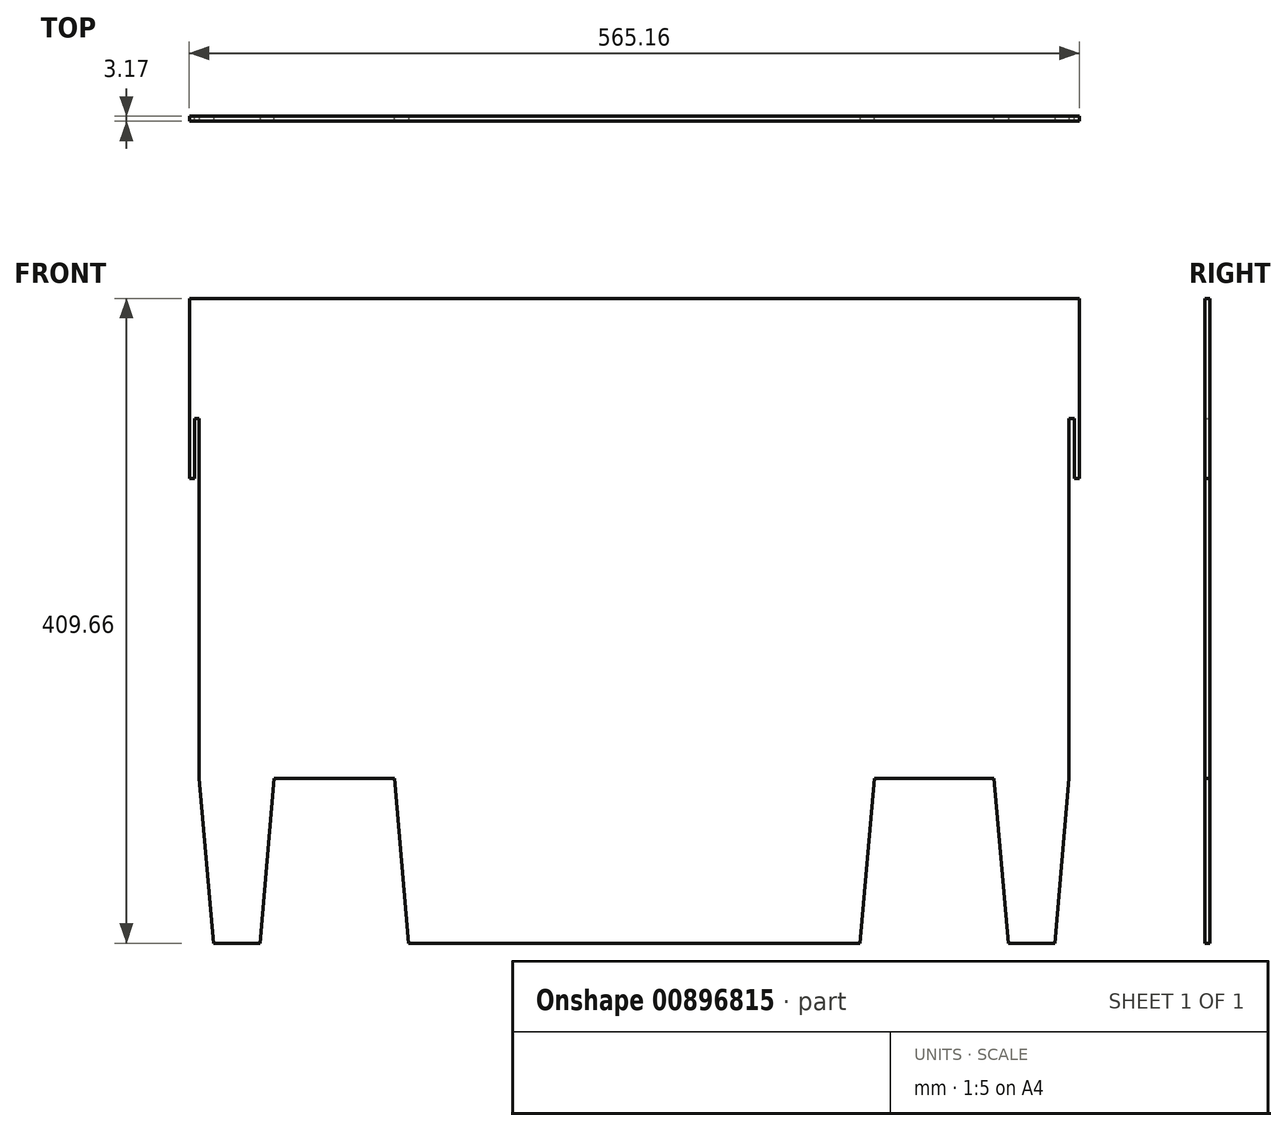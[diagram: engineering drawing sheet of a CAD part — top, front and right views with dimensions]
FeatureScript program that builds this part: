
annotation { "Feature Type Name" : "Feature", "Feature Type Description" : "" }
export const myFeature = defineFeature(function(context is Context, id is Id, definition is map)
    precondition{}
    {
        {
            var Q0;
            Q0=qCreatedBy(makeId("Front.planeOp"),FACE);
            var sketch = newSketch(context, id + "F0", { "sketchPlane" : qUnion([Q0])});
            skLineSegment(sketch, "E0.bottom", {"start": v(276.23, -304.8) * mm, "end": v(228.6, -304.8) * mm});
            skLineSegment(sketch, "E0.left", {"start": v(276.23, -304.8) * mm, "end": v(276.23, 190.5) * mm});
            skLineSegment(sketch, "E0.right", {"start": v(-276.23, -304.8) * mm, "end": v(-276.23, 190.5) * mm});
            skPoint(sketch, "E0.middle", {"position": v(0, 0) * mm});
            skLineSegment(sketch, "E1.top", {"start": v(-228.6, -38.1) * mm, "end": v(-152.4, -38.1) * mm});
            skLineSegment(sketch, "E1.left", {"start": v(-228.6, -304.8) * mm, "end": v(-228.6, -38.1) * mm});
            skLineSegment(sketch, "E1.right", {"start": v(-152.4, -304.8) * mm, "end": v(-152.4, -38.1) * mm});
            skLineSegment(sketch, "E2.top", {"start": v(152.4, -38.1) * mm, "end": v(228.6, -38.1) * mm});
            skLineSegment(sketch, "E2.left", {"start": v(152.4, -304.8) * mm, "end": v(152.4, -38.1) * mm});
            skLineSegment(sketch, "E2.right", {"start": v(228.6, -304.8) * mm, "end": v(228.6, -38.1) * mm});
            skLineSegment(sketch, "E3.trimOffspring", {"start": v(-228.6, -304.8) * mm, "end": v(-276.23, -304.8) * mm});
            skLineSegment(sketch, "E4.trimOffspring", {"start": v(152.4, -304.8) * mm, "end": v(-152.4, -304.8) * mm});
            skLineSegment(sketch, "E5.bottom", {"start": v(276.23, 266.7) * mm, "end": v(-276.23, 266.7) * mm});
            skPoint(sketch, "E0.top.start.orphan", {"position": v(276.22, 304.8) * mm});
            skPoint(sketch, "E6.orphan", {"position": v(-276.23, 304.8) * mm});
            skLineSegment(sketch, "E7.bottom", {"start": v(276.23, 266.7) * mm, "end": v(279.4, 266.7) * mm});
            skLineSegment(sketch, "E7.top", {"start": v(276.23, 190.5) * mm, "end": v(279.4, 190.5) * mm});
            skLineSegment(sketch, "E7.right", {"start": v(279.4, 266.7) * mm, "end": v(279.4, 190.5) * mm});
            skLineSegment(sketch, "E8.bottom", {"start": v(-276.23, 266.7) * mm, "end": v(-279.4, 266.7) * mm});
            skLineSegment(sketch, "E8.left", {"start": v(-276.23, 190.5) * mm, "end": v(-276.23, 185.04) * mm});
            skLineSegment(sketch, "E8.right", {"start": v(-279.4, 266.7) * mm, "end": v(-279.4, 190.5) * mm});
            skLineSegment(sketch, "E9", {"start": v(-279.4, 190.5) * mm, "end": v(-276.23, 190.5) * mm});
            skSolve(sketch);
        }
        {
            var Q0;
            Q0 = qSketchRegion(id + "F0", true);
            extrude(context, id + "F1", {"entities" : qUnion([Q0]), "depth" : 3.17 * mm, "offsetDistance" : 25.4 * mm});
        }
        {
            var Q0;
            Q0=makeQuery(id+"F1.opExtrude","CAP_FACE",FACE,{"disambiguationData":[OSD([sQuery(id+"F0.wireOp",EDGE,"E0.bottom"),sQuery(id+"F0.wireOp",EDGE,"E0.left"),sQuery(id+"F0.wireOp",EDGE,"E0.right"),sQuery(id+"F0.wireOp",EDGE,"E1.top"),sQuery(id+"F0.wireOp",EDGE,"E1.left"),sQuery(id+"F0.wireOp",EDGE,"E1.right"),sQuery(id+"F0.wireOp",EDGE,"E2.top"),sQuery(id+"F0.wireOp",EDGE,"E2.left"),sQuery(id+"F0.wireOp",EDGE,"E2.right"),sQuery(id+"F0.wireOp",EDGE,"E3.trimOffspring"),sQuery(id+"F0.wireOp",EDGE,"E4.trimOffspring"),sQuery(id+"F0.wireOp",EDGE,"E5.bottom"),sQuery(id+"F0.wireOp",EDGE,"E7.bottom"),sQuery(id+"F0.wireOp",EDGE,"E7.top"),sQuery(id+"F0.wireOp",EDGE,"E7.right"),sQuery(id+"F0.wireOp",EDGE,"E8.bottom"),sQuery(id+"F0.wireOp",EDGE,"E8.left"),sQuery(id+"F0.wireOp",EDGE,"E8.right"),sQuery(id+"F0.wireOp",EDGE,"E9")])],"isStart":false});
            var sketch = newSketch(context, id + "F2", { "sketchPlane" : qUnion([Q0])});
            skLineSegment(sketch, "E10.0.0", {"start": v(-276.23, 190.5) * mm, "end": v(-276.23, -304.8) * mm, "construction": true});
            skLineSegment(sketch, "E10.0.1", {"start": v(-276.23, -304.8) * mm, "end": v(-228.6, -304.8) * mm, "construction": true});
            skLineSegment(sketch, "E10.0.2", {"start": v(-228.6, -304.8) * mm, "end": v(-228.6, -38.1) * mm, "construction": true});
            skLineSegment(sketch, "E10.0.3", {"start": v(-228.6, -38.1) * mm, "end": v(-152.4, -38.1) * mm, "construction": true});
            skLineSegment(sketch, "E10.0.4", {"start": v(-152.4, -38.1) * mm, "end": v(-152.4, -304.8) * mm, "construction": true});
            skLineSegment(sketch, "E10.0.5", {"start": v(-152.4, -304.8) * mm, "end": v(152.4, -304.8) * mm, "construction": true});
            skLineSegment(sketch, "E10.0.6", {"start": v(152.4, -304.8) * mm, "end": v(152.4, -38.1) * mm, "construction": true});
            skLineSegment(sketch, "E10.0.7", {"start": v(152.4, -38.1) * mm, "end": v(228.6, -38.1) * mm, "construction": true});
            skLineSegment(sketch, "E10.0.8", {"start": v(228.6, -38.1) * mm, "end": v(228.6, -304.8) * mm, "construction": true});
            skLineSegment(sketch, "E10.0.9", {"start": v(228.6, -304.8) * mm, "end": v(276.23, -304.8) * mm, "construction": true});
            skLineSegment(sketch, "E10.0.10", {"start": v(276.23, -304.8) * mm, "end": v(276.23, 190.5) * mm, "construction": true});
            skLineSegment(sketch, "E10.0.11", {"start": v(276.23, 190.5) * mm, "end": v(279.4, 190.5) * mm, "construction": true});
            skLineSegment(sketch, "E10.0.12", {"start": v(279.4, 190.5) * mm, "end": v(279.4, 266.7) * mm, "construction": true});
            skLineSegment(sketch, "E10.0.13", {"start": v(279.4, 266.7) * mm, "end": v(-279.4, 266.7) * mm, "construction": true});
            skLineSegment(sketch, "E10.0.14", {"start": v(-279.4, 266.7) * mm, "end": v(-279.4, 190.5) * mm, "construction": true});
            skLineSegment(sketch, "E10.0.15", {"start": v(-279.4, 190.5) * mm, "end": v(-276.23, 190.5) * mm, "construction": true});
            skLineSegment(sketch, "E11.bottom", {"start": v(279.4, 266.7) * mm, "end": v(282.57, 266.7) * mm});
            skLineSegment(sketch, "E11.top", {"start": v(279.4, 152.4) * mm, "end": v(282.57, 152.4) * mm});
            skLineSegment(sketch, "E11.left", {"start": v(279.4, 266.7) * mm, "end": v(279.4, 152.4) * mm});
            skLineSegment(sketch, "E11.right", {"start": v(282.57, 266.7) * mm, "end": v(282.57, 152.4) * mm});
            skLineSegment(sketch, "E12.bottom", {"start": v(-279.4, 266.7) * mm, "end": v(-282.58, 266.7) * mm});
            skLineSegment(sketch, "E12.top", {"start": v(-279.4, 152.4) * mm, "end": v(-282.58, 152.4) * mm});
            skLineSegment(sketch, "E12.left", {"start": v(-279.4, 266.7) * mm, "end": v(-279.4, 152.4) * mm});
            skLineSegment(sketch, "E12.right", {"start": v(-282.58, 266.7) * mm, "end": v(-282.58, 152.4) * mm});
            skSolve(sketch);
        }
        {
            var Q0;
            Q0 = qSketchRegion(id + "F2", true);
            var Q1;
            Q1=makeQuery(id+"F1.opExtrude","CAP_FACE",FACE,{"disambiguationData":[OSD([sQuery(id+"F0.wireOp",EDGE,"E0.bottom"),sQuery(id+"F0.wireOp",EDGE,"E0.left"),sQuery(id+"F0.wireOp",EDGE,"E0.right"),sQuery(id+"F0.wireOp",EDGE,"E1.top"),sQuery(id+"F0.wireOp",EDGE,"E1.left"),sQuery(id+"F0.wireOp",EDGE,"E1.right"),sQuery(id+"F0.wireOp",EDGE,"E2.top"),sQuery(id+"F0.wireOp",EDGE,"E2.left"),sQuery(id+"F0.wireOp",EDGE,"E2.right"),sQuery(id+"F0.wireOp",EDGE,"E3.trimOffspring"),sQuery(id+"F0.wireOp",EDGE,"E4.trimOffspring"),sQuery(id+"F0.wireOp",EDGE,"E5.bottom"),sQuery(id+"F0.wireOp",EDGE,"E7.bottom"),sQuery(id+"F0.wireOp",EDGE,"E7.top"),sQuery(id+"F0.wireOp",EDGE,"E7.right"),sQuery(id+"F0.wireOp",EDGE,"E8.bottom"),sQuery(id+"F0.wireOp",EDGE,"E8.left"),sQuery(id+"F0.wireOp",EDGE,"E8.right"),sQuery(id+"F0.wireOp",EDGE,"E9")])],"isStart":true});
            extrude(context, id + "F3", {"entities" : qUnion([Q0]), "operationType" : NewBodyOperationType.ADD, "endBound" : BoundingType.UP_TO_SURFACE, "oppositeDirection" : true, "depth" : 25.4 * mm, "endBoundEntityFace" : qUnion([Q1]), "offsetDistance" : 25.4 * mm});
        }
        {
            var Q0;
            Q0=makeQuery(id+"F3.boolean.opBoolean","MERGE",FACE,{"derivedFrom":[makeQuery(id+"F1.opExtrude","CAP_FACE",FACE,{"disambiguationData":[OSD([sQuery(id+"F0.wireOp",EDGE,"E0.bottom"),sQuery(id+"F0.wireOp",EDGE,"E0.left"),sQuery(id+"F0.wireOp",EDGE,"E0.right"),sQuery(id+"F0.wireOp",EDGE,"E1.top"),sQuery(id+"F0.wireOp",EDGE,"E1.left"),sQuery(id+"F0.wireOp",EDGE,"E1.right"),sQuery(id+"F0.wireOp",EDGE,"E2.top"),sQuery(id+"F0.wireOp",EDGE,"E2.left"),sQuery(id+"F0.wireOp",EDGE,"E2.right"),sQuery(id+"F0.wireOp",EDGE,"E3.trimOffspring"),sQuery(id+"F0.wireOp",EDGE,"E4.trimOffspring"),sQuery(id+"F0.wireOp",EDGE,"E5.bottom"),sQuery(id+"F0.wireOp",EDGE,"E7.bottom"),sQuery(id+"F0.wireOp",EDGE,"E7.top"),sQuery(id+"F0.wireOp",EDGE,"E7.right"),sQuery(id+"F0.wireOp",EDGE,"E8.bottom"),sQuery(id+"F0.wireOp",EDGE,"E8.left"),sQuery(id+"F0.wireOp",EDGE,"E8.right"),sQuery(id+"F0.wireOp",EDGE,"E9")])],"isStart":false}),makeQuery(id+"F3.opExtrude","CAP_FACE",FACE,{"disambiguationData":[OSD([sQuery(id+"F2.wireOp",EDGE,"E11.bottom"),sQuery(id+"F2.wireOp",EDGE,"E11.top"),sQuery(id+"F2.wireOp",EDGE,"E11.left"),sQuery(id+"F2.wireOp",EDGE,"E11.right")])],"isStart":true}),makeQuery(id+"F3.opExtrude","CAP_FACE",FACE,{"disambiguationData":[OSD([sQuery(id+"F2.wireOp",EDGE,"E12.bottom"),sQuery(id+"F2.wireOp",EDGE,"E12.top"),sQuery(id+"F2.wireOp",EDGE,"E12.left"),sQuery(id+"F2.wireOp",EDGE,"E12.right")])],"isStart":true})]});
            var sketch = newSketch(context, id + "F4", { "sketchPlane" : qUnion([Q0])});
            skLineSegment(sketch, "E13.0.0", {"start": v(-276.23, 190.5) * mm, "end": v(-276.23, -304.8) * mm, "construction": true});
            skLineSegment(sketch, "E13.0.1", {"start": v(-276.23, -304.8) * mm, "end": v(-228.6, -304.8) * mm, "construction": true});
            skLineSegment(sketch, "E13.0.2", {"start": v(-228.6, -304.8) * mm, "end": v(-228.6, -38.1) * mm, "construction": true});
            skLineSegment(sketch, "E13.0.3", {"start": v(-228.6, -38.1) * mm, "end": v(-152.4, -38.1) * mm, "construction": true});
            skLineSegment(sketch, "E13.0.4", {"start": v(-152.4, -38.1) * mm, "end": v(-152.4, -304.8) * mm, "construction": true});
            skLineSegment(sketch, "E13.0.5", {"start": v(-152.4, -304.8) * mm, "end": v(152.4, -304.8) * mm, "construction": true});
            skLineSegment(sketch, "E13.0.6", {"start": v(152.4, -304.8) * mm, "end": v(152.4, -38.1) * mm, "construction": true});
            skLineSegment(sketch, "E13.0.7", {"start": v(152.4, -38.1) * mm, "end": v(228.6, -38.1) * mm, "construction": true});
            skLineSegment(sketch, "E13.0.8", {"start": v(228.6, -38.1) * mm, "end": v(228.6, -304.8) * mm, "construction": true});
            skLineSegment(sketch, "E13.0.9", {"start": v(228.6, -304.8) * mm, "end": v(276.23, -304.8) * mm, "construction": true});
            skLineSegment(sketch, "E13.0.10", {"start": v(276.23, -304.8) * mm, "end": v(276.23, 190.5) * mm, "construction": true});
            skLineSegment(sketch, "E13.0.11", {"start": v(276.23, 190.5) * mm, "end": v(279.4, 190.5) * mm, "construction": true});
            skLineSegment(sketch, "E13.0.12", {"start": v(279.4, 190.5) * mm, "end": v(279.4, 152.4) * mm, "construction": true});
            skLineSegment(sketch, "E13.0.13", {"start": v(279.4, 152.4) * mm, "end": v(282.57, 152.4) * mm, "construction": true});
            skLineSegment(sketch, "E13.0.14", {"start": v(282.57, 152.4) * mm, "end": v(282.57, 266.7) * mm, "construction": true});
            skLineSegment(sketch, "E13.0.15", {"start": v(282.57, 266.7) * mm, "end": v(-282.58, 266.7) * mm, "construction": true});
            skLineSegment(sketch, "E13.0.16", {"start": v(-282.58, 266.7) * mm, "end": v(-282.58, 152.4) * mm, "construction": true});
            skLineSegment(sketch, "E13.0.17", {"start": v(-282.58, 152.4) * mm, "end": v(-279.4, 152.4) * mm, "construction": true});
            skLineSegment(sketch, "E13.0.18", {"start": v(-279.4, 152.4) * mm, "end": v(-279.4, 190.5) * mm, "construction": true});
            skLineSegment(sketch, "E13.0.19", {"start": v(-279.4, 190.5) * mm, "end": v(-276.23, 190.5) * mm, "construction": true});
            skLineSegment(sketch, "E14", {"start": v(-228.6, -38.1) * mm, "end": v(-237.77, -142.96) * mm});
            skLineSegment(sketch, "E15", {"start": v(-251.93, -304.8) * mm, "end": v(-228.6, -304.8) * mm});
            skLineSegment(sketch, "E16", {"start": v(-228.6, -304.8) * mm, "end": v(-228.6, -38.1) * mm});
            skLineSegment(sketch, "E17", {"start": v(-152.4, -38.1) * mm, "end": v(-145.74, -114.2) * mm});
            skLineSegment(sketch, "E18", {"start": v(145.74, -114.2) * mm, "end": v(152.4, -38.1) * mm});
            skLineSegment(sketch, "E19", {"start": v(152.4, -38.1) * mm, "end": v(152.4, -304.8) * mm});
            skLineSegment(sketch, "E20", {"start": v(152.4, -304.8) * mm, "end": v(-152.4, -304.8) * mm});
            skLineSegment(sketch, "E21", {"start": v(-152.4, -304.8) * mm, "end": v(-152.4, -38.1) * mm});
            skLineSegment(sketch, "E22", {"start": v(228.6, -38.1) * mm, "end": v(237.77, -142.96) * mm});
            skLineSegment(sketch, "E23", {"start": v(251.93, -304.8) * mm, "end": v(228.6, -304.8) * mm});
            skLineSegment(sketch, "E24", {"start": v(228.6, -304.8) * mm, "end": v(228.6, -38.1) * mm});
            skLineSegment(sketch, "E25", {"start": v(276.23, -38.1) * mm, "end": v(267.05, -142.96) * mm});
            skLineSegment(sketch, "E26", {"start": v(252.9, -304.8) * mm, "end": v(276.23, -304.8) * mm});
            skLineSegment(sketch, "E27", {"start": v(276.23, -304.8) * mm, "end": v(276.23, -38.1) * mm});
            skLineSegment(sketch, "E28", {"start": v(-276.23, -38.1) * mm, "end": v(-276.23, -304.8) * mm});
            skLineSegment(sketch, "E29", {"start": v(-276.23, -304.8) * mm, "end": v(-252.9, -304.8) * mm});
            skLineSegment(sketch, "E30", {"start": v(-267.05, -142.96) * mm, "end": v(-276.23, -38.1) * mm});
            skLineSegment(sketch, "E31.bottom", {"start": v(-267.05, -142.96) * mm, "end": v(-237.77, -142.96) * mm});
            skLineSegment(sketch, "E31.top", {"start": v(-276.23, -304.8) * mm, "end": v(276.23, -304.8) * mm});
            skLineSegment(sketch, "E31.left", {"start": v(-276.23, -142.96) * mm, "end": v(-276.23, -304.8) * mm});
            skLineSegment(sketch, "E31.right", {"start": v(276.23, -142.96) * mm, "end": v(276.23, -304.8) * mm});
            skLineSegment(sketch, "E32", {"start": v(-145.74, -114.2) * mm, "end": v(-143.23, -142.96) * mm});
            skLineSegment(sketch, "E33", {"start": v(145.74, -114.2) * mm, "end": v(143.23, -142.96) * mm});
            skLineSegment(sketch, "E34.trimOffspring", {"start": v(-143.23, -142.96) * mm, "end": v(143.23, -142.96) * mm});
            skLineSegment(sketch, "E35.trimOffspring", {"start": v(152.4, -142.96) * mm, "end": v(228.6, -142.96) * mm});
            skLineSegment(sketch, "E36.trimOffspring", {"start": v(237.77, -142.96) * mm, "end": v(267.05, -142.96) * mm});
            skLineSegment(sketch, "E37.trimOffspring", {"start": v(-228.6, -142.96) * mm, "end": v(-152.4, -142.96) * mm});
            skSolve(sketch);
        }
        {
            var Q0;
            Q0 = qSketchRegion(id + "F4", true);
            extrude(context, id + "F5", {"entities" : qUnion([Q0]), "operationType" : NewBodyOperationType.REMOVE, "endBound" : BoundingType.THROUGH_ALL, "oppositeDirection" : true, "depth" : 25.4 * mm, "offsetDistance" : 25.4 * mm});
        }
    });
